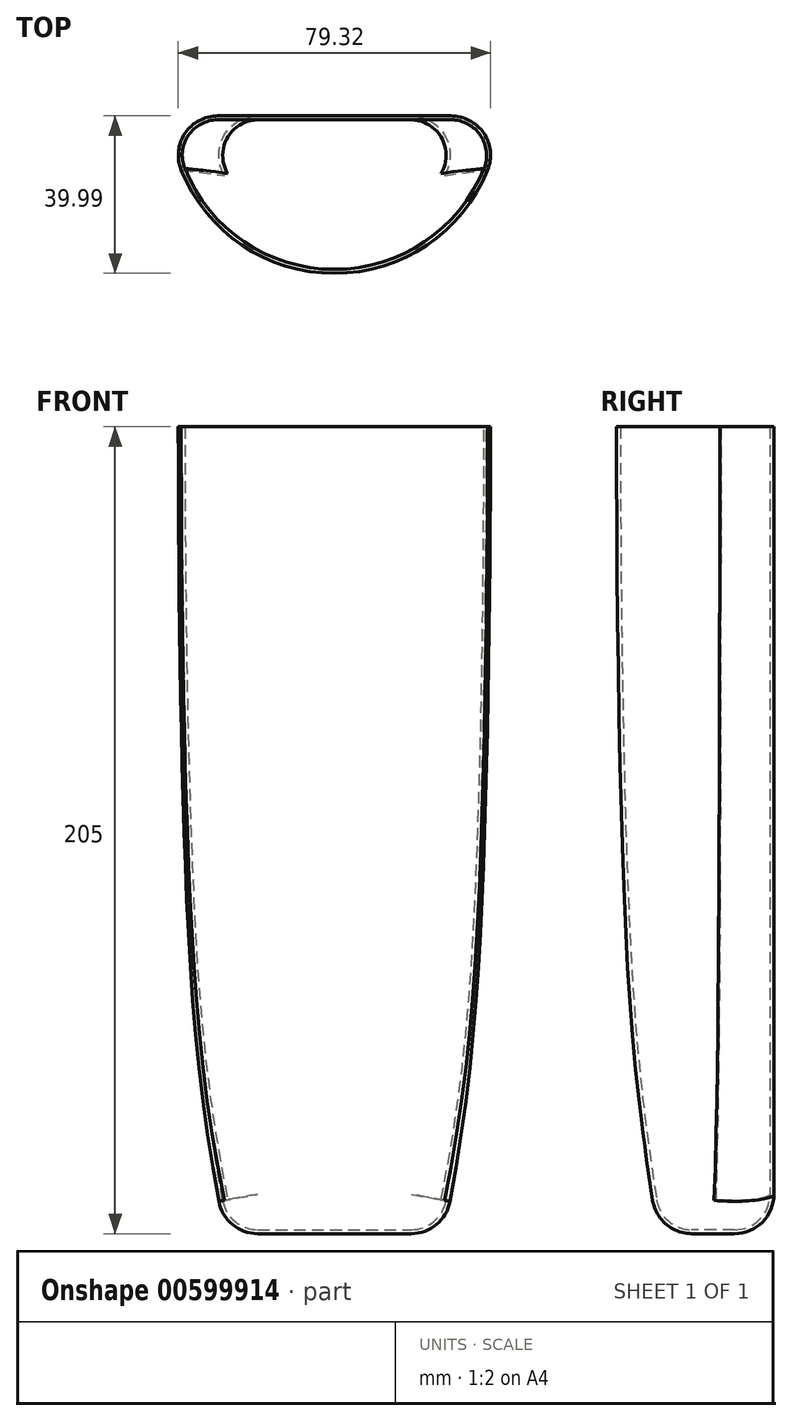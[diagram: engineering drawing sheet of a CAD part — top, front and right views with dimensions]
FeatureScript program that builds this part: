
annotation { "Feature Type Name" : "Feature", "Feature Type Description" : "" }
export const myFeature = defineFeature(function(context is Context, id is Id, definition is map)
    precondition{}
    {
        {
            var Q0;
            Q0=qCreatedBy(makeId("Front.planeOp"),FACE);
            var sketch = newSketch(context, id + "F0", { "sketchPlane" : qUnion([Q0])});
            skFitSpline(sketch, "E0", {"points": [v(31.5, 15) * mm, v(39, 80) * mm, v(42, 220) * mm], "startDerivative": vector(16.6, 111.32) * mm, "endDerivative": vector(0, 81.62) * mm});
            skPoint(sketch, "E1.end.orphan", {"position": v(0, 220) * mm});
            skLineSegment(sketch, "E2", {"start": v(0, 220) * mm, "end": v(0, 15) * mm});
            skPoint(sketch, "E3.end.orphan", {"position": v(31.5, 0) * mm});
            skLineSegment(sketch, "E4", {"start": v(0, 15) * mm, "end": v(31.5, 15) * mm});
            skLineSegment(sketch, "E5", {"start": v(0, 220) * mm, "end": v(42, 220) * mm});
            skSolve(sketch);
        }
        {
            var Q0;
            Q0=makeQuery(id+"F0.imprint","IMPRINT",FACE,{"disambiguationData":[TD([[makeQuery(id+"F0.imprint","IMPRINT",EDGE,{"derivedFrom":sQuery(id+"F0.wireOp",EDGE,"E0")}),1.0]])]});
            var Q1;
            Q1=sQuery(id+"F0.wireOp",EDGE,"E2");
            revolve(context, id + "F1", {"entities" : qUnion([Q0]), "axis" : qUnion([Q1]), "revolveType" : RevolveType.ONE_DIRECTION, "angle" : 180 * degree});
        }
        {
            var Q0;
            Q0=makeQuery(id+"F1.opRevolve","SWEPT_FACE",FACE,{"disambiguationData":[OSD([sQuery(id+"F0.wireOp",EDGE,"E5")])]});
            var sketch = newSketch(context, id + "F2", { "sketchPlane" : qUnion([Q0])});
            skLineSegment(sketch, "E6", {"start": v(-41.95, -2) * mm, "end": v(41.95, -2) * mm});
            skLineSegment(sketch, "E7", {"start": v(-42, 0) * mm, "end": v(42, 0) * mm});
            skArc(sketch, "E8", {"start": v(-42, 0) * mm, "mid": v(-41.99, -1) * mm, "end": v(-41.95, -2) * mm});
            skArc(sketch, "E9", {"start": v(-42, 0) * mm, "mid": v(0, -42) * mm, "end": v(42, 0) * mm});
            skSolve(sketch);
        }
        {
            var Q0;
            {var subQ0=sQuery(id+"F2.wireOp",EDGE,"E6");Q0=makeQuery(id+"F2.imprint","IMPRINT",FACE,{"disambiguationData":[TD([[makeQuery(id+"F2.imprint","IMPRINT",EDGE,{"derivedFrom":subQ0}),1.0]])]});}
            extrude(context, id + "F3", {"entities" : qUnion([Q0]), "operationType" : NewBodyOperationType.REMOVE, "endBound" : BoundingType.THROUGH_ALL, "oppositeDirection" : true, "depth" : 25 * mm, "offsetDistance" : 25 * mm});
        }
        {
            var Q0;
            Q0=makeQuery(id+"F3.boolean.opBoolean","INTERSECT",EDGE,{"disambiguationData":[OD(1.0)],"derivedFrom":[makeQuery(id+"F1.opRevolve","SWEPT_FACE",FACE,{"disambiguationData":[OSD([sQuery(id+"F0.wireOp",EDGE,"E0")])]}),makeQuery(id+"F3.opExtrude","SWEPT_FACE",FACE,{"disambiguationData":[OSD([sQuery(id+"F2.wireOp",EDGE,"E6")])]})]});
            var Q1;
            Q1=makeQuery(id+"F3.boolean.opBoolean","INTERSECT",EDGE,{"disambiguationData":[OD(0.0)],"derivedFrom":[makeQuery(id+"F1.opRevolve","SWEPT_FACE",FACE,{"disambiguationData":[OSD([sQuery(id+"F0.wireOp",EDGE,"E0")])]}),makeQuery(id+"F3.opExtrude","SWEPT_FACE",FACE,{"disambiguationData":[OSD([sQuery(id+"F2.wireOp",EDGE,"E6")])]})]});
            var Q2;
            Q2=makeQuery(id+"F3.boolean.opBoolean","INTERSECT",EDGE,{"derivedFrom":[makeQuery(id+"F1.opRevolve","SWEPT_FACE",FACE,{"disambiguationData":[OSD([sQuery(id+"F0.wireOp",EDGE,"E4")])]}),makeQuery(id+"F3.opExtrude","SWEPT_FACE",FACE,{"disambiguationData":[OSD([sQuery(id+"F2.wireOp",EDGE,"E6")])]})]});
            var Q3;
            Q3=makeQuery(id+"F1.opRevolve","SWEPT_EDGE",EDGE,{"disambiguationData":[OSD([sQuery(id+"F0.wireOp",EDGE,"E0"),sQuery(id+"F0.wireOp",EDGE,"E4")])]});
            fillet(context, id + "F4", {"entities" : qUnion([Q0, Q1, Q2, Q3]), "radius" : 10 * mm, "tangentPropagation" : true, "allowEdgeOverflow" : false});
        }
        {
            var Q0;
            Q0=makeQuery(id+"F1.opRevolve","SWEPT_FACE",FACE,{"disambiguationData":[OSD([sQuery(id+"F0.wireOp",EDGE,"E5")])]});
            shell(context, id + "F5", {"entities" : qUnion([Q0]), "thickness" : 1 * mm});
        }
    });
